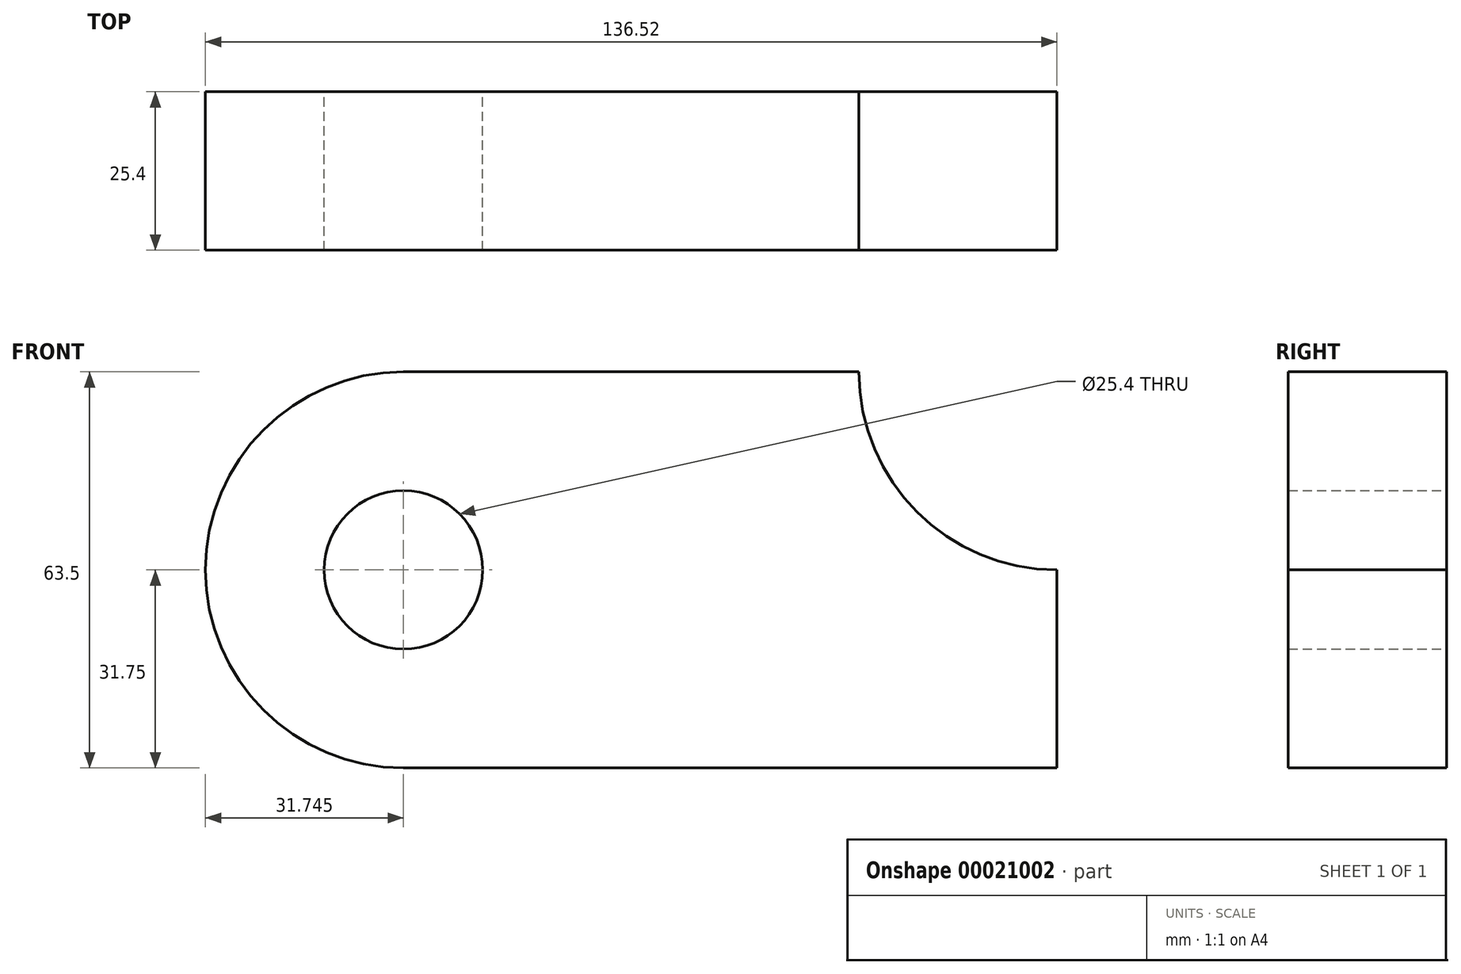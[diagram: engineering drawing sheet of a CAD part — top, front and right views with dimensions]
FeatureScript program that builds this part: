
annotation { "Feature Type Name" : "Feature", "Feature Type Description" : "" }
export const myFeature = defineFeature(function(context is Context, id is Id, definition is map)
    precondition{}
    {
        {
            var Q0;
            Q0=qCreatedBy(makeId("Front.planeOp"),FACE);
            var sketch = newSketch(context, id + "F0", { "sketchPlane" : qUnion([Q0])});
            skLineSegment(sketch, "E0.bottom", {"start": v(-104.78, 63.5) * mm, "end": v(0, 63.5) * mm});
            skLineSegment(sketch, "E0.top", {"start": v(-104.77, 0) * mm, "end": v(0, 0) * mm});
            skLineSegment(sketch, "E0.left", {"start": v(-104.78, 63.5) * mm, "end": v(-104.78, 0) * mm});
            skLineSegment(sketch, "E0.right", {"start": v(0, 63.5) * mm, "end": v(0, 0) * mm});
            skCircle(sketch, "E1", {"center": v(-104.78, 31.75) * mm, "radius": 31.75 * mm});
            skCircle(sketch, "E2", {"center": v(0, 63.5) * mm, "radius": 31.75 * mm});
            skCircle(sketch, "E3", {"center": v(-104.78, 31.75) * mm, "radius": 12.7 * mm});
            skSolve(sketch);
        }
        {
            var Q0;
            {var subQ6=sQuery(id+"F0.wireOp",EDGE,"E0.top");Q0=makeQuery(id+"F0.imprint","IMPRINT",FACE,{"disambiguationData":[TD([[makeQuery(id+"F0.imprint","IMPRINT",EDGE,{"derivedFrom":subQ6}),1.0]])]});}
            var Q1;
            {var subQ1=sQuery(id+"F0.wireOp",EDGE,"E0.left");var subQ4=sQuery(id+"F0.wireOp",EDGE,"E3");var subQ6=makeQuery(id+"F0.imprint","INTERSECT",VERTEX,{"disambiguationData":[OD(0.0)],"derivedFrom":[subQ1,subQ4]});Q1=makeQuery(id+"F0.imprint","IMPRINT",FACE,{"disambiguationData":[TD([[makeQuery(id+"F0.imprint","IMPRINT",EDGE,{"disambiguationData":[TD([[subQ6,-1.0]])],"derivedFrom":subQ4}),-1.0]])]});}
            var Q2;
            {var subQ0=sQuery(id+"F0.wireOp",EDGE,"E3");var subQ1=sQuery(id+"F0.wireOp",EDGE,"E0.left");var subQ3=makeQuery(id+"F0.imprint","INTERSECT",VERTEX,{"disambiguationData":[OD(0.0)],"derivedFrom":[subQ1,subQ0]});Q2=makeQuery(id+"F0.imprint","IMPRINT",FACE,{"disambiguationData":[TD([[makeQuery(id+"F0.imprint","IMPRINT",EDGE,{"disambiguationData":[TD([[subQ3,1.0]])],"derivedFrom":subQ0}),-1.0]])]});}
            extrude(context, id + "F1", {"entities" : qUnion([Q0, Q1, Q2]), "depth" : 25.4 * mm});
        }
    });
